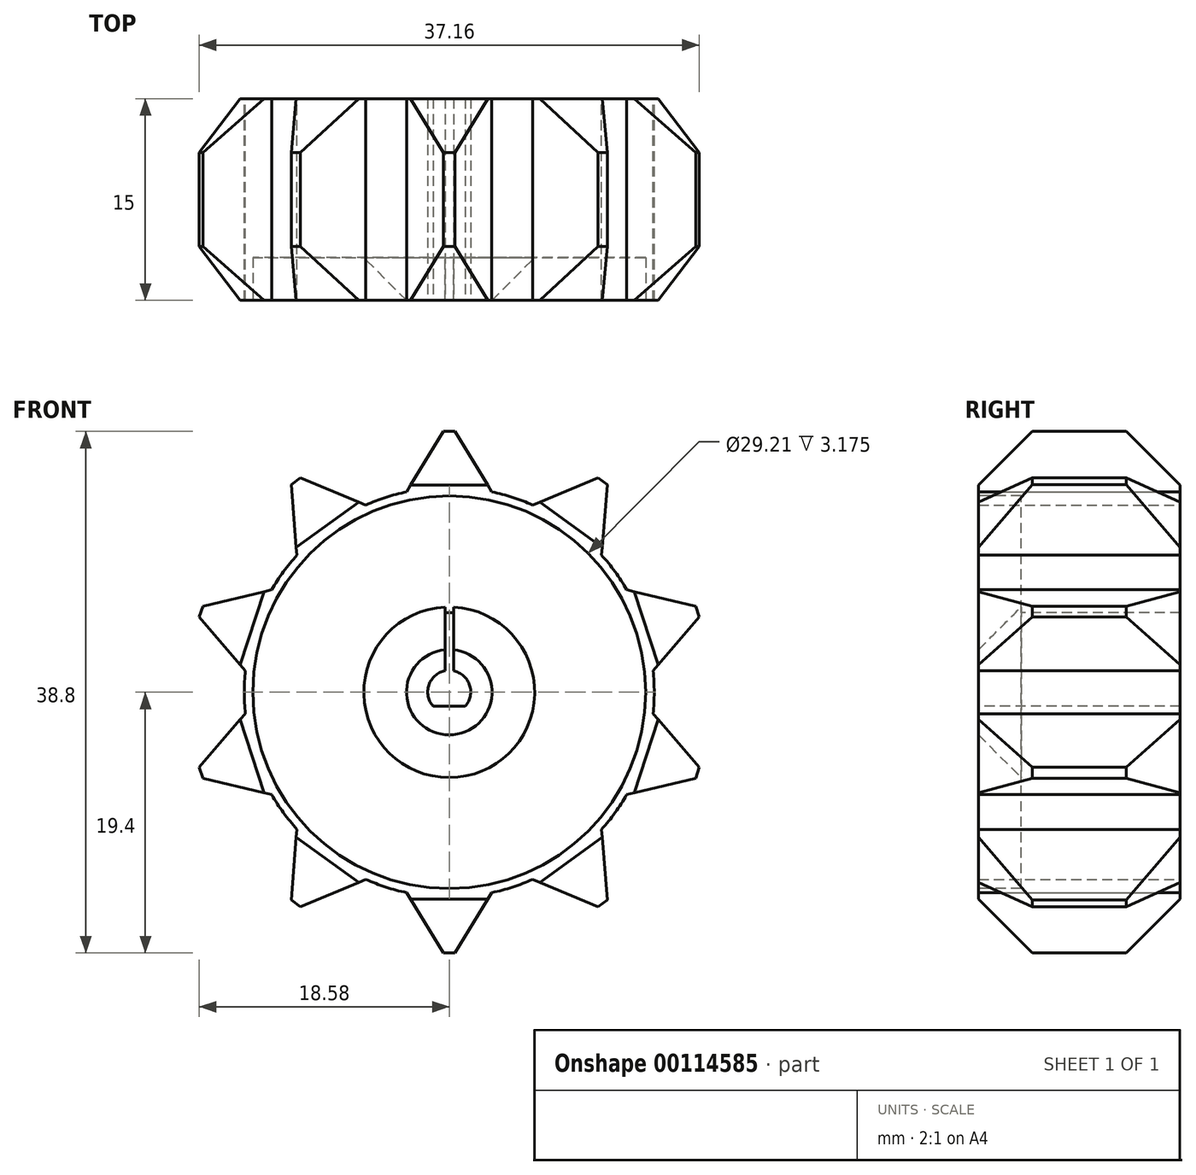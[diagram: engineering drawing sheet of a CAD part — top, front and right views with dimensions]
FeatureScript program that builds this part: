
annotation { "Feature Type Name" : "Feature", "Feature Type Description" : "" }
export const myFeature = defineFeature(function(context is Context, id is Id, definition is map)
    precondition{}
    {
        {
            var Q0;
            Q0=qCreatedBy(makeId("Front.planeOp"),FACE);
            var sketch = newSketch(context, id + "F0", { "sketchPlane" : qUnion([Q0])});
            skCircle(sketch, "E0", {"center": v(0, 0) * mm, "radius": 15.24 * mm});
            skLineSegment(sketch, "E1", {"start": v(0, 20.1) * mm, "end": v(3.17, 14.9) * mm});
            skLineSegment(sketch, "E2.MirrorCS", {"start": v(0, 20.1) * mm, "end": v(-3.17, 14.9) * mm});
            skLineSegment(sketch, "E3.1.0", {"start": v(-11.81, 16.26) * mm, "end": v(-11.32, 10.2) * mm});
            skLineSegment(sketch, "E3.1.1", {"start": v(-11.81, 16.26) * mm, "end": v(-6.2, 13.92) * mm});
            skLineSegment(sketch, "E3.2.0", {"start": v(-19.12, 6.21) * mm, "end": v(-15.16, 1.6) * mm});
            skLineSegment(sketch, "E3.2.1", {"start": v(-19.12, 6.21) * mm, "end": v(-13.2, 7.62) * mm});
            skLineSegment(sketch, "E4.2.3.0", {"start": v(-19.12, -6.21) * mm, "end": v(-13.2, -7.62) * mm});
            skLineSegment(sketch, "E4.3.3.0", {"start": v(-19.12, -6.21) * mm, "end": v(-15.16, -1.6) * mm});
            skLineSegment(sketch, "E4.2.4.0", {"start": v(-11.81, -16.26) * mm, "end": v(-6.2, -13.92) * mm});
            skLineSegment(sketch, "E4.3.4.0", {"start": v(-11.81, -16.26) * mm, "end": v(-11.32, -10.2) * mm});
            skLineSegment(sketch, "E4.2.5.0", {"start": v(0, -20.1) * mm, "end": v(3.17, -14.9) * mm});
            skLineSegment(sketch, "E4.3.5.0", {"start": v(0, -20.1) * mm, "end": v(-3.17, -14.9) * mm});
            skLineSegment(sketch, "E5.2.6.0", {"start": v(11.81, -16.26) * mm, "end": v(11.32, -10.2) * mm});
            skLineSegment(sketch, "E5.3.6.0", {"start": v(11.81, -16.26) * mm, "end": v(6.2, -13.92) * mm});
            skLineSegment(sketch, "E5.2.7.0", {"start": v(19.12, -6.21) * mm, "end": v(15.16, -1.6) * mm});
            skLineSegment(sketch, "E5.3.7.0", {"start": v(19.12, -6.21) * mm, "end": v(13.2, -7.62) * mm});
            skLineSegment(sketch, "E6.2.8.0", {"start": v(19.12, 6.21) * mm, "end": v(13.2, 7.62) * mm});
            skLineSegment(sketch, "E6.3.8.0", {"start": v(19.12, 6.21) * mm, "end": v(15.16, 1.6) * mm});
            skLineSegment(sketch, "E6.2.9.0", {"start": v(11.81, 16.26) * mm, "end": v(6.2, 13.92) * mm});
            skLineSegment(sketch, "E6.3.9.0", {"start": v(11.81, 16.26) * mm, "end": v(11.32, 10.2) * mm});
            skSolve(sketch);
        }
        {
            var Q0;
            {var subQ0=sQuery(id+"F0.wireOp",EDGE,"E4.2.5.0");Q0=makeQuery(id+"F0.imprint","IMPRINT",FACE,{"disambiguationData":[TD([[makeQuery(id+"F0.imprint","IMPRINT",EDGE,{"derivedFrom":subQ0}),1.0]])]});}
            var Q1;
            {var subQ0=sQuery(id+"F0.wireOp",EDGE,"E1");Q1=makeQuery(id+"F0.imprint","IMPRINT",FACE,{"disambiguationData":[TD([[makeQuery(id+"F0.imprint","IMPRINT",EDGE,{"derivedFrom":subQ0}),-1.0]])]});}
            var Q2;
            {var subQ0=sQuery(id+"F0.wireOp",EDGE,"E3.1.0");Q2=makeQuery(id+"F0.imprint","IMPRINT",FACE,{"disambiguationData":[TD([[makeQuery(id+"F0.imprint","IMPRINT",EDGE,{"derivedFrom":subQ0}),1.0]])]});}
            var Q3;
            {var subQ0=sQuery(id+"F0.wireOp",EDGE,"E3.2.0");Q3=makeQuery(id+"F0.imprint","IMPRINT",FACE,{"disambiguationData":[TD([[makeQuery(id+"F0.imprint","IMPRINT",EDGE,{"derivedFrom":subQ0}),1.0]])]});}
            var Q4;
            {var subQ0=sQuery(id+"F0.wireOp",EDGE,"E4.2.3.0");Q4=makeQuery(id+"F0.imprint","IMPRINT",FACE,{"disambiguationData":[TD([[makeQuery(id+"F0.imprint","IMPRINT",EDGE,{"derivedFrom":subQ0}),1.0]])]});}
            var Q5;
            {var subQ0=sQuery(id+"F0.wireOp",EDGE,"E4.2.4.0");Q5=makeQuery(id+"F0.imprint","IMPRINT",FACE,{"disambiguationData":[TD([[makeQuery(id+"F0.imprint","IMPRINT",EDGE,{"derivedFrom":subQ0}),1.0]])]});}
            var Q6;
            {var subQ0=sQuery(id+"F0.wireOp",EDGE,"E0");var subQ3=makeQuery(id+"F0.imprint","INTERSECT",VERTEX,{"derivedFrom":[subQ0,sQuery(id+"F0.wireOp",EDGE,"E4.2.5.0")]});Q6=makeQuery(id+"F0.imprint","IMPRINT",FACE,{"disambiguationData":[TD([[makeQuery(id+"F0.imprint","IMPRINT",EDGE,{"disambiguationData":[TD([[subQ3,1.0]])],"derivedFrom":subQ0}),1.0]])]});}
            var Q7;
            {var subQ0=sQuery(id+"F0.wireOp",EDGE,"E6.2.9.0");Q7=makeQuery(id+"F0.imprint","IMPRINT",FACE,{"disambiguationData":[TD([[makeQuery(id+"F0.imprint","IMPRINT",EDGE,{"derivedFrom":subQ0}),1.0]])]});}
            var Q8;
            {var subQ0=sQuery(id+"F0.wireOp",EDGE,"E6.2.8.0");Q8=makeQuery(id+"F0.imprint","IMPRINT",FACE,{"disambiguationData":[TD([[makeQuery(id+"F0.imprint","IMPRINT",EDGE,{"derivedFrom":subQ0}),1.0]])]});}
            var Q9;
            {var subQ0=sQuery(id+"F0.wireOp",EDGE,"E5.2.7.0");Q9=makeQuery(id+"F0.imprint","IMPRINT",FACE,{"disambiguationData":[TD([[makeQuery(id+"F0.imprint","IMPRINT",EDGE,{"derivedFrom":subQ0}),1.0]])]});}
            var Q10;
            {var subQ0=sQuery(id+"F0.wireOp",EDGE,"E5.2.6.0");Q10=makeQuery(id+"F0.imprint","IMPRINT",FACE,{"disambiguationData":[TD([[makeQuery(id+"F0.imprint","IMPRINT",EDGE,{"derivedFrom":subQ0}),1.0]])]});}
            extrude(context, id + "F1", {"entities" : qUnion([Q0, Q1, Q2, Q3, Q4, Q5, Q6, Q7, Q8, Q9, Q10]), "depth" : 15 * mm});
        }
        {
            var Q0;
            Q0=makeQuery(id+"F1.opExtrude","SWEPT_EDGE",EDGE,{"disambiguationData":[OSD([sQuery(id+"F0.wireOp",EDGE,"E4.2.5.0"),sQuery(id+"F0.wireOp",EDGE,"E4.3.5.0")])]});
            var Q1;
            Q1=makeQuery(id+"F1.opExtrude","SWEPT_EDGE",EDGE,{"disambiguationData":[OSD([sQuery(id+"F0.wireOp",EDGE,"E1"),sQuery(id+"F0.wireOp",EDGE,"E2.MirrorCS")])]});
            var Q2;
            Q2=makeQuery(id+"F1.opExtrude","SWEPT_EDGE",EDGE,{"disambiguationData":[OSD([sQuery(id+"F0.wireOp",EDGE,"E4.2.4.0"),sQuery(id+"F0.wireOp",EDGE,"E4.3.4.0")])]});
            var Q3;
            Q3=makeQuery(id+"F1.opExtrude","SWEPT_EDGE",EDGE,{"disambiguationData":[OSD([sQuery(id+"F0.wireOp",EDGE,"E4.2.3.0"),sQuery(id+"F0.wireOp",EDGE,"E4.3.3.0")])]});
            var Q4;
            Q4=makeQuery(id+"F1.opExtrude","SWEPT_EDGE",EDGE,{"disambiguationData":[OSD([sQuery(id+"F0.wireOp",EDGE,"E3.2.0"),sQuery(id+"F0.wireOp",EDGE,"E3.2.1")])]});
            var Q5;
            Q5=makeQuery(id+"F1.opExtrude","SWEPT_EDGE",EDGE,{"disambiguationData":[OSD([sQuery(id+"F0.wireOp",EDGE,"E3.1.0"),sQuery(id+"F0.wireOp",EDGE,"E3.1.1")])]});
            var Q6;
            Q6=makeQuery(id+"F1.opExtrude","SWEPT_EDGE",EDGE,{"disambiguationData":[OSD([sQuery(id+"F0.wireOp",EDGE,"E6.2.9.0"),sQuery(id+"F0.wireOp",EDGE,"E6.3.9.0")])]});
            var Q7;
            Q7=makeQuery(id+"F1.opExtrude","SWEPT_EDGE",EDGE,{"disambiguationData":[OSD([sQuery(id+"F0.wireOp",EDGE,"E6.2.8.0"),sQuery(id+"F0.wireOp",EDGE,"E6.3.8.0")])]});
            var Q8;
            Q8=makeQuery(id+"F1.opExtrude","SWEPT_EDGE",EDGE,{"disambiguationData":[OSD([sQuery(id+"F0.wireOp",EDGE,"E5.2.7.0"),sQuery(id+"F0.wireOp",EDGE,"E5.3.7.0")])]});
            var Q9;
            Q9=makeQuery(id+"F1.opExtrude","SWEPT_EDGE",EDGE,{"disambiguationData":[OSD([sQuery(id+"F0.wireOp",EDGE,"E5.2.6.0"),sQuery(id+"F0.wireOp",EDGE,"E5.3.6.0")])]});
            chamfer(context, id + "F2", {"entities" : qUnion([Q0, Q1, Q2, Q3, Q4, Q5, Q6, Q7, Q8, Q9]), "width" : .5 * mm, "tangentPropagation" : true});
        }
        {
            var Q0;
            {var subQ0=sQuery(id+"F0.wireOp",EDGE,"E3.1.1");var subQ1=sQuery(id+"F0.wireOp",EDGE,"E3.1.0");Q0=makeQuery(id+"F2.opChamfer","BLEND_EDGE",EDGE,{"blendedFrom":[makeQuery(id+"F1.opExtrude","SWEPT_EDGE",EDGE,{"disambiguationData":[OSD([subQ1,subQ0])]}),makeQuery(id+"F1.opExtrude","CAP_FACE",FACE,{"disambiguationData":[OSD([sQuery(id+"F0.wireOp",EDGE,"E0"),sQuery(id+"F0.wireOp",EDGE,"E1"),sQuery(id+"F0.wireOp",EDGE,"E2.MirrorCS"),subQ1,subQ0,sQuery(id+"F0.wireOp",EDGE,"E3.2.0"),sQuery(id+"F0.wireOp",EDGE,"E3.2.1"),sQuery(id+"F0.wireOp",EDGE,"E4.2.3.0"),sQuery(id+"F0.wireOp",EDGE,"E4.3.3.0"),sQuery(id+"F0.wireOp",EDGE,"E4.2.4.0"),sQuery(id+"F0.wireOp",EDGE,"E4.3.4.0"),sQuery(id+"F0.wireOp",EDGE,"E4.2.5.0"),sQuery(id+"F0.wireOp",EDGE,"E4.3.5.0")])],"isStart":false})],"blendedInto":[makeQuery(id+"F1.opExtrude","CAP_FACE",FACE,{"disambiguationData":[OSD([sQuery(id+"F0.wireOp",EDGE,"E0"),sQuery(id+"F0.wireOp",EDGE,"E1"),sQuery(id+"F0.wireOp",EDGE,"E2.MirrorCS"),subQ1,subQ0,sQuery(id+"F0.wireOp",EDGE,"E3.2.0"),sQuery(id+"F0.wireOp",EDGE,"E3.2.1"),sQuery(id+"F0.wireOp",EDGE,"E4.2.3.0"),sQuery(id+"F0.wireOp",EDGE,"E4.3.3.0"),sQuery(id+"F0.wireOp",EDGE,"E4.2.4.0"),sQuery(id+"F0.wireOp",EDGE,"E4.3.4.0"),sQuery(id+"F0.wireOp",EDGE,"E4.2.5.0"),sQuery(id+"F0.wireOp",EDGE,"E4.3.5.0")])],"isStart":false})]});}
            var Q1;
            {var subQ0=sQuery(id+"F0.wireOp",EDGE,"E3.1.1");var subQ1=sQuery(id+"F0.wireOp",EDGE,"E3.1.0");Q1=makeQuery(id+"F2.opChamfer","BLEND_EDGE",EDGE,{"blendedFrom":[makeQuery(id+"F1.opExtrude","SWEPT_EDGE",EDGE,{"disambiguationData":[OSD([subQ1,subQ0])]}),makeQuery(id+"F1.opExtrude","CAP_FACE",FACE,{"disambiguationData":[OSD([sQuery(id+"F0.wireOp",EDGE,"E0"),sQuery(id+"F0.wireOp",EDGE,"E1"),sQuery(id+"F0.wireOp",EDGE,"E2.MirrorCS"),subQ1,subQ0,sQuery(id+"F0.wireOp",EDGE,"E3.2.0"),sQuery(id+"F0.wireOp",EDGE,"E3.2.1"),sQuery(id+"F0.wireOp",EDGE,"E4.2.3.0"),sQuery(id+"F0.wireOp",EDGE,"E4.3.3.0"),sQuery(id+"F0.wireOp",EDGE,"E4.2.4.0"),sQuery(id+"F0.wireOp",EDGE,"E4.3.4.0"),sQuery(id+"F0.wireOp",EDGE,"E4.2.5.0"),sQuery(id+"F0.wireOp",EDGE,"E4.3.5.0")])],"isStart":true})],"blendedInto":[makeQuery(id+"F1.opExtrude","CAP_FACE",FACE,{"disambiguationData":[OSD([sQuery(id+"F0.wireOp",EDGE,"E0"),sQuery(id+"F0.wireOp",EDGE,"E1"),sQuery(id+"F0.wireOp",EDGE,"E2.MirrorCS"),subQ1,subQ0,sQuery(id+"F0.wireOp",EDGE,"E3.2.0"),sQuery(id+"F0.wireOp",EDGE,"E3.2.1"),sQuery(id+"F0.wireOp",EDGE,"E4.2.3.0"),sQuery(id+"F0.wireOp",EDGE,"E4.3.3.0"),sQuery(id+"F0.wireOp",EDGE,"E4.2.4.0"),sQuery(id+"F0.wireOp",EDGE,"E4.3.4.0"),sQuery(id+"F0.wireOp",EDGE,"E4.2.5.0"),sQuery(id+"F0.wireOp",EDGE,"E4.3.5.0")])],"isStart":true})]});}
            var Q2;
            {var subQ0=sQuery(id+"F0.wireOp",EDGE,"E2.MirrorCS");var subQ1=sQuery(id+"F0.wireOp",EDGE,"E1");Q2=makeQuery(id+"F2.opChamfer","BLEND_EDGE",EDGE,{"blendedFrom":[makeQuery(id+"F1.opExtrude","SWEPT_EDGE",EDGE,{"disambiguationData":[OSD([subQ1,subQ0])]}),makeQuery(id+"F1.opExtrude","CAP_FACE",FACE,{"disambiguationData":[OSD([sQuery(id+"F0.wireOp",EDGE,"E0"),subQ1,subQ0,sQuery(id+"F0.wireOp",EDGE,"E3.1.0"),sQuery(id+"F0.wireOp",EDGE,"E3.1.1"),sQuery(id+"F0.wireOp",EDGE,"E3.2.0"),sQuery(id+"F0.wireOp",EDGE,"E3.2.1"),sQuery(id+"F0.wireOp",EDGE,"E4.2.3.0"),sQuery(id+"F0.wireOp",EDGE,"E4.3.3.0"),sQuery(id+"F0.wireOp",EDGE,"E4.2.4.0"),sQuery(id+"F0.wireOp",EDGE,"E4.3.4.0"),sQuery(id+"F0.wireOp",EDGE,"E4.2.5.0"),sQuery(id+"F0.wireOp",EDGE,"E4.3.5.0")])],"isStart":true})],"blendedInto":[makeQuery(id+"F1.opExtrude","CAP_FACE",FACE,{"disambiguationData":[OSD([sQuery(id+"F0.wireOp",EDGE,"E0"),subQ1,subQ0,sQuery(id+"F0.wireOp",EDGE,"E3.1.0"),sQuery(id+"F0.wireOp",EDGE,"E3.1.1"),sQuery(id+"F0.wireOp",EDGE,"E3.2.0"),sQuery(id+"F0.wireOp",EDGE,"E3.2.1"),sQuery(id+"F0.wireOp",EDGE,"E4.2.3.0"),sQuery(id+"F0.wireOp",EDGE,"E4.3.3.0"),sQuery(id+"F0.wireOp",EDGE,"E4.2.4.0"),sQuery(id+"F0.wireOp",EDGE,"E4.3.4.0"),sQuery(id+"F0.wireOp",EDGE,"E4.2.5.0"),sQuery(id+"F0.wireOp",EDGE,"E4.3.5.0")])],"isStart":true})]});}
            var Q3;
            {var subQ0=sQuery(id+"F0.wireOp",EDGE,"E2.MirrorCS");var subQ1=sQuery(id+"F0.wireOp",EDGE,"E1");Q3=makeQuery(id+"F2.opChamfer","BLEND_EDGE",EDGE,{"blendedFrom":[makeQuery(id+"F1.opExtrude","SWEPT_EDGE",EDGE,{"disambiguationData":[OSD([subQ1,subQ0])]}),makeQuery(id+"F1.opExtrude","CAP_FACE",FACE,{"disambiguationData":[OSD([sQuery(id+"F0.wireOp",EDGE,"E0"),subQ1,subQ0,sQuery(id+"F0.wireOp",EDGE,"E3.1.0"),sQuery(id+"F0.wireOp",EDGE,"E3.1.1"),sQuery(id+"F0.wireOp",EDGE,"E3.2.0"),sQuery(id+"F0.wireOp",EDGE,"E3.2.1"),sQuery(id+"F0.wireOp",EDGE,"E4.2.3.0"),sQuery(id+"F0.wireOp",EDGE,"E4.3.3.0"),sQuery(id+"F0.wireOp",EDGE,"E4.2.4.0"),sQuery(id+"F0.wireOp",EDGE,"E4.3.4.0"),sQuery(id+"F0.wireOp",EDGE,"E4.2.5.0"),sQuery(id+"F0.wireOp",EDGE,"E4.3.5.0")])],"isStart":false})],"blendedInto":[makeQuery(id+"F1.opExtrude","CAP_FACE",FACE,{"disambiguationData":[OSD([sQuery(id+"F0.wireOp",EDGE,"E0"),subQ1,subQ0,sQuery(id+"F0.wireOp",EDGE,"E3.1.0"),sQuery(id+"F0.wireOp",EDGE,"E3.1.1"),sQuery(id+"F0.wireOp",EDGE,"E3.2.0"),sQuery(id+"F0.wireOp",EDGE,"E3.2.1"),sQuery(id+"F0.wireOp",EDGE,"E4.2.3.0"),sQuery(id+"F0.wireOp",EDGE,"E4.3.3.0"),sQuery(id+"F0.wireOp",EDGE,"E4.2.4.0"),sQuery(id+"F0.wireOp",EDGE,"E4.3.4.0"),sQuery(id+"F0.wireOp",EDGE,"E4.2.5.0"),sQuery(id+"F0.wireOp",EDGE,"E4.3.5.0")])],"isStart":false})]});}
            var Q4;
            {var subQ0=sQuery(id+"F0.wireOp",EDGE,"E4.3.5.0");var subQ1=sQuery(id+"F0.wireOp",EDGE,"E4.2.5.0");Q4=makeQuery(id+"F2.opChamfer","BLEND_EDGE",EDGE,{"blendedFrom":[makeQuery(id+"F1.opExtrude","SWEPT_EDGE",EDGE,{"disambiguationData":[OSD([subQ1,subQ0])]}),makeQuery(id+"F1.opExtrude","CAP_FACE",FACE,{"disambiguationData":[OSD([sQuery(id+"F0.wireOp",EDGE,"E0"),sQuery(id+"F0.wireOp",EDGE,"E1"),sQuery(id+"F0.wireOp",EDGE,"E2.MirrorCS"),sQuery(id+"F0.wireOp",EDGE,"E3.1.0"),sQuery(id+"F0.wireOp",EDGE,"E3.1.1"),sQuery(id+"F0.wireOp",EDGE,"E3.2.0"),sQuery(id+"F0.wireOp",EDGE,"E3.2.1"),sQuery(id+"F0.wireOp",EDGE,"E4.2.3.0"),sQuery(id+"F0.wireOp",EDGE,"E4.3.3.0"),sQuery(id+"F0.wireOp",EDGE,"E4.2.4.0"),sQuery(id+"F0.wireOp",EDGE,"E4.3.4.0"),subQ1,subQ0])],"isStart":false})],"blendedInto":[makeQuery(id+"F1.opExtrude","CAP_FACE",FACE,{"disambiguationData":[OSD([sQuery(id+"F0.wireOp",EDGE,"E0"),sQuery(id+"F0.wireOp",EDGE,"E1"),sQuery(id+"F0.wireOp",EDGE,"E2.MirrorCS"),sQuery(id+"F0.wireOp",EDGE,"E3.1.0"),sQuery(id+"F0.wireOp",EDGE,"E3.1.1"),sQuery(id+"F0.wireOp",EDGE,"E3.2.0"),sQuery(id+"F0.wireOp",EDGE,"E3.2.1"),sQuery(id+"F0.wireOp",EDGE,"E4.2.3.0"),sQuery(id+"F0.wireOp",EDGE,"E4.3.3.0"),sQuery(id+"F0.wireOp",EDGE,"E4.2.4.0"),sQuery(id+"F0.wireOp",EDGE,"E4.3.4.0"),subQ1,subQ0])],"isStart":false})]});}
            var Q5;
            {var subQ0=sQuery(id+"F0.wireOp",EDGE,"E4.3.4.0");var subQ1=sQuery(id+"F0.wireOp",EDGE,"E4.2.4.0");Q5=makeQuery(id+"F2.opChamfer","BLEND_EDGE",EDGE,{"blendedFrom":[makeQuery(id+"F1.opExtrude","SWEPT_EDGE",EDGE,{"disambiguationData":[OSD([subQ1,subQ0])]}),makeQuery(id+"F1.opExtrude","CAP_FACE",FACE,{"disambiguationData":[OSD([sQuery(id+"F0.wireOp",EDGE,"E0"),sQuery(id+"F0.wireOp",EDGE,"E1"),sQuery(id+"F0.wireOp",EDGE,"E2.MirrorCS"),sQuery(id+"F0.wireOp",EDGE,"E3.1.0"),sQuery(id+"F0.wireOp",EDGE,"E3.1.1"),sQuery(id+"F0.wireOp",EDGE,"E3.2.0"),sQuery(id+"F0.wireOp",EDGE,"E3.2.1"),sQuery(id+"F0.wireOp",EDGE,"E4.2.3.0"),sQuery(id+"F0.wireOp",EDGE,"E4.3.3.0"),subQ1,subQ0,sQuery(id+"F0.wireOp",EDGE,"E4.2.5.0"),sQuery(id+"F0.wireOp",EDGE,"E4.3.5.0")])],"isStart":false})],"blendedInto":[makeQuery(id+"F1.opExtrude","CAP_FACE",FACE,{"disambiguationData":[OSD([sQuery(id+"F0.wireOp",EDGE,"E0"),sQuery(id+"F0.wireOp",EDGE,"E1"),sQuery(id+"F0.wireOp",EDGE,"E2.MirrorCS"),sQuery(id+"F0.wireOp",EDGE,"E3.1.0"),sQuery(id+"F0.wireOp",EDGE,"E3.1.1"),sQuery(id+"F0.wireOp",EDGE,"E3.2.0"),sQuery(id+"F0.wireOp",EDGE,"E3.2.1"),sQuery(id+"F0.wireOp",EDGE,"E4.2.3.0"),sQuery(id+"F0.wireOp",EDGE,"E4.3.3.0"),subQ1,subQ0,sQuery(id+"F0.wireOp",EDGE,"E4.2.5.0"),sQuery(id+"F0.wireOp",EDGE,"E4.3.5.0")])],"isStart":false})]});}
            var Q6;
            {var subQ0=sQuery(id+"F0.wireOp",EDGE,"E4.3.3.0");var subQ1=sQuery(id+"F0.wireOp",EDGE,"E4.2.3.0");Q6=makeQuery(id+"F2.opChamfer","BLEND_EDGE",EDGE,{"blendedFrom":[makeQuery(id+"F1.opExtrude","SWEPT_EDGE",EDGE,{"disambiguationData":[OSD([subQ1,subQ0])]}),makeQuery(id+"F1.opExtrude","CAP_FACE",FACE,{"disambiguationData":[OSD([sQuery(id+"F0.wireOp",EDGE,"E0"),sQuery(id+"F0.wireOp",EDGE,"E1"),sQuery(id+"F0.wireOp",EDGE,"E2.MirrorCS"),sQuery(id+"F0.wireOp",EDGE,"E3.1.0"),sQuery(id+"F0.wireOp",EDGE,"E3.1.1"),sQuery(id+"F0.wireOp",EDGE,"E3.2.0"),sQuery(id+"F0.wireOp",EDGE,"E3.2.1"),subQ1,subQ0,sQuery(id+"F0.wireOp",EDGE,"E4.2.4.0"),sQuery(id+"F0.wireOp",EDGE,"E4.3.4.0"),sQuery(id+"F0.wireOp",EDGE,"E4.2.5.0"),sQuery(id+"F0.wireOp",EDGE,"E4.3.5.0")])],"isStart":false})],"blendedInto":[makeQuery(id+"F1.opExtrude","CAP_FACE",FACE,{"disambiguationData":[OSD([sQuery(id+"F0.wireOp",EDGE,"E0"),sQuery(id+"F0.wireOp",EDGE,"E1"),sQuery(id+"F0.wireOp",EDGE,"E2.MirrorCS"),sQuery(id+"F0.wireOp",EDGE,"E3.1.0"),sQuery(id+"F0.wireOp",EDGE,"E3.1.1"),sQuery(id+"F0.wireOp",EDGE,"E3.2.0"),sQuery(id+"F0.wireOp",EDGE,"E3.2.1"),subQ1,subQ0,sQuery(id+"F0.wireOp",EDGE,"E4.2.4.0"),sQuery(id+"F0.wireOp",EDGE,"E4.3.4.0"),sQuery(id+"F0.wireOp",EDGE,"E4.2.5.0"),sQuery(id+"F0.wireOp",EDGE,"E4.3.5.0")])],"isStart":false})]});}
            var Q7;
            {var subQ0=sQuery(id+"F0.wireOp",EDGE,"E3.2.1");var subQ1=sQuery(id+"F0.wireOp",EDGE,"E3.2.0");Q7=makeQuery(id+"F2.opChamfer","BLEND_EDGE",EDGE,{"blendedFrom":[makeQuery(id+"F1.opExtrude","SWEPT_EDGE",EDGE,{"disambiguationData":[OSD([subQ1,subQ0])]}),makeQuery(id+"F1.opExtrude","CAP_FACE",FACE,{"disambiguationData":[OSD([sQuery(id+"F0.wireOp",EDGE,"E0"),sQuery(id+"F0.wireOp",EDGE,"E1"),sQuery(id+"F0.wireOp",EDGE,"E2.MirrorCS"),sQuery(id+"F0.wireOp",EDGE,"E3.1.0"),sQuery(id+"F0.wireOp",EDGE,"E3.1.1"),subQ1,subQ0,sQuery(id+"F0.wireOp",EDGE,"E4.2.3.0"),sQuery(id+"F0.wireOp",EDGE,"E4.3.3.0"),sQuery(id+"F0.wireOp",EDGE,"E4.2.4.0"),sQuery(id+"F0.wireOp",EDGE,"E4.3.4.0"),sQuery(id+"F0.wireOp",EDGE,"E4.2.5.0"),sQuery(id+"F0.wireOp",EDGE,"E4.3.5.0")])],"isStart":false})],"blendedInto":[makeQuery(id+"F1.opExtrude","CAP_FACE",FACE,{"disambiguationData":[OSD([sQuery(id+"F0.wireOp",EDGE,"E0"),sQuery(id+"F0.wireOp",EDGE,"E1"),sQuery(id+"F0.wireOp",EDGE,"E2.MirrorCS"),sQuery(id+"F0.wireOp",EDGE,"E3.1.0"),sQuery(id+"F0.wireOp",EDGE,"E3.1.1"),subQ1,subQ0,sQuery(id+"F0.wireOp",EDGE,"E4.2.3.0"),sQuery(id+"F0.wireOp",EDGE,"E4.3.3.0"),sQuery(id+"F0.wireOp",EDGE,"E4.2.4.0"),sQuery(id+"F0.wireOp",EDGE,"E4.3.4.0"),sQuery(id+"F0.wireOp",EDGE,"E4.2.5.0"),sQuery(id+"F0.wireOp",EDGE,"E4.3.5.0")])],"isStart":false})]});}
            var Q8;
            {var subQ0=sQuery(id+"F0.wireOp",EDGE,"E3.2.1");var subQ1=sQuery(id+"F0.wireOp",EDGE,"E3.2.0");Q8=makeQuery(id+"F2.opChamfer","BLEND_EDGE",EDGE,{"blendedFrom":[makeQuery(id+"F1.opExtrude","SWEPT_EDGE",EDGE,{"disambiguationData":[OSD([subQ1,subQ0])]}),makeQuery(id+"F1.opExtrude","CAP_FACE",FACE,{"disambiguationData":[OSD([sQuery(id+"F0.wireOp",EDGE,"E0"),sQuery(id+"F0.wireOp",EDGE,"E1"),sQuery(id+"F0.wireOp",EDGE,"E2.MirrorCS"),sQuery(id+"F0.wireOp",EDGE,"E3.1.0"),sQuery(id+"F0.wireOp",EDGE,"E3.1.1"),subQ1,subQ0,sQuery(id+"F0.wireOp",EDGE,"E4.2.3.0"),sQuery(id+"F0.wireOp",EDGE,"E4.3.3.0"),sQuery(id+"F0.wireOp",EDGE,"E4.2.4.0"),sQuery(id+"F0.wireOp",EDGE,"E4.3.4.0"),sQuery(id+"F0.wireOp",EDGE,"E4.2.5.0"),sQuery(id+"F0.wireOp",EDGE,"E4.3.5.0")])],"isStart":true})],"blendedInto":[makeQuery(id+"F1.opExtrude","CAP_FACE",FACE,{"disambiguationData":[OSD([sQuery(id+"F0.wireOp",EDGE,"E0"),sQuery(id+"F0.wireOp",EDGE,"E1"),sQuery(id+"F0.wireOp",EDGE,"E2.MirrorCS"),sQuery(id+"F0.wireOp",EDGE,"E3.1.0"),sQuery(id+"F0.wireOp",EDGE,"E3.1.1"),subQ1,subQ0,sQuery(id+"F0.wireOp",EDGE,"E4.2.3.0"),sQuery(id+"F0.wireOp",EDGE,"E4.3.3.0"),sQuery(id+"F0.wireOp",EDGE,"E4.2.4.0"),sQuery(id+"F0.wireOp",EDGE,"E4.3.4.0"),sQuery(id+"F0.wireOp",EDGE,"E4.2.5.0"),sQuery(id+"F0.wireOp",EDGE,"E4.3.5.0")])],"isStart":true})]});}
            var Q9;
            {var subQ0=sQuery(id+"F0.wireOp",EDGE,"E4.3.3.0");var subQ1=sQuery(id+"F0.wireOp",EDGE,"E4.2.3.0");Q9=makeQuery(id+"F2.opChamfer","BLEND_EDGE",EDGE,{"blendedFrom":[makeQuery(id+"F1.opExtrude","SWEPT_EDGE",EDGE,{"disambiguationData":[OSD([subQ1,subQ0])]}),makeQuery(id+"F1.opExtrude","CAP_FACE",FACE,{"disambiguationData":[OSD([sQuery(id+"F0.wireOp",EDGE,"E0"),sQuery(id+"F0.wireOp",EDGE,"E1"),sQuery(id+"F0.wireOp",EDGE,"E2.MirrorCS"),sQuery(id+"F0.wireOp",EDGE,"E3.1.0"),sQuery(id+"F0.wireOp",EDGE,"E3.1.1"),sQuery(id+"F0.wireOp",EDGE,"E3.2.0"),sQuery(id+"F0.wireOp",EDGE,"E3.2.1"),subQ1,subQ0,sQuery(id+"F0.wireOp",EDGE,"E4.2.4.0"),sQuery(id+"F0.wireOp",EDGE,"E4.3.4.0"),sQuery(id+"F0.wireOp",EDGE,"E4.2.5.0"),sQuery(id+"F0.wireOp",EDGE,"E4.3.5.0")])],"isStart":true})],"blendedInto":[makeQuery(id+"F1.opExtrude","CAP_FACE",FACE,{"disambiguationData":[OSD([sQuery(id+"F0.wireOp",EDGE,"E0"),sQuery(id+"F0.wireOp",EDGE,"E1"),sQuery(id+"F0.wireOp",EDGE,"E2.MirrorCS"),sQuery(id+"F0.wireOp",EDGE,"E3.1.0"),sQuery(id+"F0.wireOp",EDGE,"E3.1.1"),sQuery(id+"F0.wireOp",EDGE,"E3.2.0"),sQuery(id+"F0.wireOp",EDGE,"E3.2.1"),subQ1,subQ0,sQuery(id+"F0.wireOp",EDGE,"E4.2.4.0"),sQuery(id+"F0.wireOp",EDGE,"E4.3.4.0"),sQuery(id+"F0.wireOp",EDGE,"E4.2.5.0"),sQuery(id+"F0.wireOp",EDGE,"E4.3.5.0")])],"isStart":true})]});}
            var Q10;
            {var subQ0=sQuery(id+"F0.wireOp",EDGE,"E4.3.4.0");var subQ1=sQuery(id+"F0.wireOp",EDGE,"E4.2.4.0");Q10=makeQuery(id+"F2.opChamfer","BLEND_EDGE",EDGE,{"blendedFrom":[makeQuery(id+"F1.opExtrude","SWEPT_EDGE",EDGE,{"disambiguationData":[OSD([subQ1,subQ0])]}),makeQuery(id+"F1.opExtrude","CAP_FACE",FACE,{"disambiguationData":[OSD([sQuery(id+"F0.wireOp",EDGE,"E0"),sQuery(id+"F0.wireOp",EDGE,"E1"),sQuery(id+"F0.wireOp",EDGE,"E2.MirrorCS"),sQuery(id+"F0.wireOp",EDGE,"E3.1.0"),sQuery(id+"F0.wireOp",EDGE,"E3.1.1"),sQuery(id+"F0.wireOp",EDGE,"E3.2.0"),sQuery(id+"F0.wireOp",EDGE,"E3.2.1"),sQuery(id+"F0.wireOp",EDGE,"E4.2.3.0"),sQuery(id+"F0.wireOp",EDGE,"E4.3.3.0"),subQ1,subQ0,sQuery(id+"F0.wireOp",EDGE,"E4.2.5.0"),sQuery(id+"F0.wireOp",EDGE,"E4.3.5.0")])],"isStart":true})],"blendedInto":[makeQuery(id+"F1.opExtrude","CAP_FACE",FACE,{"disambiguationData":[OSD([sQuery(id+"F0.wireOp",EDGE,"E0"),sQuery(id+"F0.wireOp",EDGE,"E1"),sQuery(id+"F0.wireOp",EDGE,"E2.MirrorCS"),sQuery(id+"F0.wireOp",EDGE,"E3.1.0"),sQuery(id+"F0.wireOp",EDGE,"E3.1.1"),sQuery(id+"F0.wireOp",EDGE,"E3.2.0"),sQuery(id+"F0.wireOp",EDGE,"E3.2.1"),sQuery(id+"F0.wireOp",EDGE,"E4.2.3.0"),sQuery(id+"F0.wireOp",EDGE,"E4.3.3.0"),subQ1,subQ0,sQuery(id+"F0.wireOp",EDGE,"E4.2.5.0"),sQuery(id+"F0.wireOp",EDGE,"E4.3.5.0")])],"isStart":true})]});}
            var Q11;
            {var subQ0=sQuery(id+"F0.wireOp",EDGE,"E4.3.5.0");var subQ1=sQuery(id+"F0.wireOp",EDGE,"E4.2.5.0");Q11=makeQuery(id+"F2.opChamfer","BLEND_EDGE",EDGE,{"blendedFrom":[makeQuery(id+"F1.opExtrude","SWEPT_EDGE",EDGE,{"disambiguationData":[OSD([subQ1,subQ0])]}),makeQuery(id+"F1.opExtrude","CAP_FACE",FACE,{"disambiguationData":[OSD([sQuery(id+"F0.wireOp",EDGE,"E0"),sQuery(id+"F0.wireOp",EDGE,"E1"),sQuery(id+"F0.wireOp",EDGE,"E2.MirrorCS"),sQuery(id+"F0.wireOp",EDGE,"E3.1.0"),sQuery(id+"F0.wireOp",EDGE,"E3.1.1"),sQuery(id+"F0.wireOp",EDGE,"E3.2.0"),sQuery(id+"F0.wireOp",EDGE,"E3.2.1"),sQuery(id+"F0.wireOp",EDGE,"E4.2.3.0"),sQuery(id+"F0.wireOp",EDGE,"E4.3.3.0"),sQuery(id+"F0.wireOp",EDGE,"E4.2.4.0"),sQuery(id+"F0.wireOp",EDGE,"E4.3.4.0"),subQ1,subQ0])],"isStart":true})],"blendedInto":[makeQuery(id+"F1.opExtrude","CAP_FACE",FACE,{"disambiguationData":[OSD([sQuery(id+"F0.wireOp",EDGE,"E0"),sQuery(id+"F0.wireOp",EDGE,"E1"),sQuery(id+"F0.wireOp",EDGE,"E2.MirrorCS"),sQuery(id+"F0.wireOp",EDGE,"E3.1.0"),sQuery(id+"F0.wireOp",EDGE,"E3.1.1"),sQuery(id+"F0.wireOp",EDGE,"E3.2.0"),sQuery(id+"F0.wireOp",EDGE,"E3.2.1"),sQuery(id+"F0.wireOp",EDGE,"E4.2.3.0"),sQuery(id+"F0.wireOp",EDGE,"E4.3.3.0"),sQuery(id+"F0.wireOp",EDGE,"E4.2.4.0"),sQuery(id+"F0.wireOp",EDGE,"E4.3.4.0"),subQ1,subQ0])],"isStart":true})]});}
            var Q12;
            {var subQ0=sQuery(id+"F0.wireOp",EDGE,"E6.3.9.0");var subQ1=sQuery(id+"F0.wireOp",EDGE,"E6.2.9.0");Q12=makeQuery(id+"F2.opChamfer","BLEND_EDGE",EDGE,{"blendedFrom":[makeQuery(id+"F1.opExtrude","SWEPT_EDGE",EDGE,{"disambiguationData":[OSD([subQ1,subQ0])]}),makeQuery(id+"F1.opExtrude","CAP_FACE",FACE,{"disambiguationData":[OSD([sQuery(id+"F0.wireOp",EDGE,"E0"),sQuery(id+"F0.wireOp",EDGE,"E1"),sQuery(id+"F0.wireOp",EDGE,"E2.MirrorCS"),sQuery(id+"F0.wireOp",EDGE,"E3.1.0"),sQuery(id+"F0.wireOp",EDGE,"E3.1.1"),sQuery(id+"F0.wireOp",EDGE,"E3.2.0"),sQuery(id+"F0.wireOp",EDGE,"E3.2.1"),sQuery(id+"F0.wireOp",EDGE,"E4.2.3.0"),sQuery(id+"F0.wireOp",EDGE,"E4.3.3.0"),sQuery(id+"F0.wireOp",EDGE,"E4.2.4.0"),sQuery(id+"F0.wireOp",EDGE,"E4.3.4.0"),sQuery(id+"F0.wireOp",EDGE,"E4.2.5.0"),sQuery(id+"F0.wireOp",EDGE,"E4.3.5.0"),sQuery(id+"F0.wireOp",EDGE,"E5.2.6.0"),sQuery(id+"F0.wireOp",EDGE,"E5.3.6.0"),sQuery(id+"F0.wireOp",EDGE,"E5.2.7.0"),sQuery(id+"F0.wireOp",EDGE,"E5.3.7.0"),sQuery(id+"F0.wireOp",EDGE,"E6.2.8.0"),sQuery(id+"F0.wireOp",EDGE,"E6.3.8.0"),subQ1,subQ0])],"isStart":false})],"blendedInto":[makeQuery(id+"F1.opExtrude","CAP_FACE",FACE,{"disambiguationData":[OSD([sQuery(id+"F0.wireOp",EDGE,"E0"),sQuery(id+"F0.wireOp",EDGE,"E1"),sQuery(id+"F0.wireOp",EDGE,"E2.MirrorCS"),sQuery(id+"F0.wireOp",EDGE,"E3.1.0"),sQuery(id+"F0.wireOp",EDGE,"E3.1.1"),sQuery(id+"F0.wireOp",EDGE,"E3.2.0"),sQuery(id+"F0.wireOp",EDGE,"E3.2.1"),sQuery(id+"F0.wireOp",EDGE,"E4.2.3.0"),sQuery(id+"F0.wireOp",EDGE,"E4.3.3.0"),sQuery(id+"F0.wireOp",EDGE,"E4.2.4.0"),sQuery(id+"F0.wireOp",EDGE,"E4.3.4.0"),sQuery(id+"F0.wireOp",EDGE,"E4.2.5.0"),sQuery(id+"F0.wireOp",EDGE,"E4.3.5.0"),sQuery(id+"F0.wireOp",EDGE,"E5.2.6.0"),sQuery(id+"F0.wireOp",EDGE,"E5.3.6.0"),sQuery(id+"F0.wireOp",EDGE,"E5.2.7.0"),sQuery(id+"F0.wireOp",EDGE,"E5.3.7.0"),sQuery(id+"F0.wireOp",EDGE,"E6.2.8.0"),sQuery(id+"F0.wireOp",EDGE,"E6.3.8.0"),subQ1,subQ0])],"isStart":false})]});}
            var Q13;
            {var subQ0=sQuery(id+"F0.wireOp",EDGE,"E6.3.8.0");var subQ1=sQuery(id+"F0.wireOp",EDGE,"E6.2.8.0");Q13=makeQuery(id+"F2.opChamfer","BLEND_EDGE",EDGE,{"blendedFrom":[makeQuery(id+"F1.opExtrude","SWEPT_EDGE",EDGE,{"disambiguationData":[OSD([subQ1,subQ0])]}),makeQuery(id+"F1.opExtrude","CAP_FACE",FACE,{"disambiguationData":[OSD([sQuery(id+"F0.wireOp",EDGE,"E0"),sQuery(id+"F0.wireOp",EDGE,"E1"),sQuery(id+"F0.wireOp",EDGE,"E2.MirrorCS"),sQuery(id+"F0.wireOp",EDGE,"E3.1.0"),sQuery(id+"F0.wireOp",EDGE,"E3.1.1"),sQuery(id+"F0.wireOp",EDGE,"E3.2.0"),sQuery(id+"F0.wireOp",EDGE,"E3.2.1"),sQuery(id+"F0.wireOp",EDGE,"E4.2.3.0"),sQuery(id+"F0.wireOp",EDGE,"E4.3.3.0"),sQuery(id+"F0.wireOp",EDGE,"E4.2.4.0"),sQuery(id+"F0.wireOp",EDGE,"E4.3.4.0"),sQuery(id+"F0.wireOp",EDGE,"E4.2.5.0"),sQuery(id+"F0.wireOp",EDGE,"E4.3.5.0"),sQuery(id+"F0.wireOp",EDGE,"E5.2.6.0"),sQuery(id+"F0.wireOp",EDGE,"E5.3.6.0"),sQuery(id+"F0.wireOp",EDGE,"E5.2.7.0"),sQuery(id+"F0.wireOp",EDGE,"E5.3.7.0"),subQ1,subQ0,sQuery(id+"F0.wireOp",EDGE,"E6.2.9.0"),sQuery(id+"F0.wireOp",EDGE,"E6.3.9.0")])],"isStart":false})],"blendedInto":[makeQuery(id+"F1.opExtrude","CAP_FACE",FACE,{"disambiguationData":[OSD([sQuery(id+"F0.wireOp",EDGE,"E0"),sQuery(id+"F0.wireOp",EDGE,"E1"),sQuery(id+"F0.wireOp",EDGE,"E2.MirrorCS"),sQuery(id+"F0.wireOp",EDGE,"E3.1.0"),sQuery(id+"F0.wireOp",EDGE,"E3.1.1"),sQuery(id+"F0.wireOp",EDGE,"E3.2.0"),sQuery(id+"F0.wireOp",EDGE,"E3.2.1"),sQuery(id+"F0.wireOp",EDGE,"E4.2.3.0"),sQuery(id+"F0.wireOp",EDGE,"E4.3.3.0"),sQuery(id+"F0.wireOp",EDGE,"E4.2.4.0"),sQuery(id+"F0.wireOp",EDGE,"E4.3.4.0"),sQuery(id+"F0.wireOp",EDGE,"E4.2.5.0"),sQuery(id+"F0.wireOp",EDGE,"E4.3.5.0"),sQuery(id+"F0.wireOp",EDGE,"E5.2.6.0"),sQuery(id+"F0.wireOp",EDGE,"E5.3.6.0"),sQuery(id+"F0.wireOp",EDGE,"E5.2.7.0"),sQuery(id+"F0.wireOp",EDGE,"E5.3.7.0"),subQ1,subQ0,sQuery(id+"F0.wireOp",EDGE,"E6.2.9.0"),sQuery(id+"F0.wireOp",EDGE,"E6.3.9.0")])],"isStart":false})]});}
            var Q14;
            {var subQ0=sQuery(id+"F0.wireOp",EDGE,"E5.3.7.0");var subQ1=sQuery(id+"F0.wireOp",EDGE,"E5.2.7.0");Q14=makeQuery(id+"F2.opChamfer","BLEND_EDGE",EDGE,{"blendedFrom":[makeQuery(id+"F1.opExtrude","SWEPT_EDGE",EDGE,{"disambiguationData":[OSD([subQ1,subQ0])]}),makeQuery(id+"F1.opExtrude","CAP_FACE",FACE,{"disambiguationData":[OSD([sQuery(id+"F0.wireOp",EDGE,"E0"),sQuery(id+"F0.wireOp",EDGE,"E1"),sQuery(id+"F0.wireOp",EDGE,"E2.MirrorCS"),sQuery(id+"F0.wireOp",EDGE,"E3.1.0"),sQuery(id+"F0.wireOp",EDGE,"E3.1.1"),sQuery(id+"F0.wireOp",EDGE,"E3.2.0"),sQuery(id+"F0.wireOp",EDGE,"E3.2.1"),sQuery(id+"F0.wireOp",EDGE,"E4.2.3.0"),sQuery(id+"F0.wireOp",EDGE,"E4.3.3.0"),sQuery(id+"F0.wireOp",EDGE,"E4.2.4.0"),sQuery(id+"F0.wireOp",EDGE,"E4.3.4.0"),sQuery(id+"F0.wireOp",EDGE,"E4.2.5.0"),sQuery(id+"F0.wireOp",EDGE,"E4.3.5.0"),sQuery(id+"F0.wireOp",EDGE,"E5.2.6.0"),sQuery(id+"F0.wireOp",EDGE,"E5.3.6.0"),subQ1,subQ0,sQuery(id+"F0.wireOp",EDGE,"E6.2.8.0"),sQuery(id+"F0.wireOp",EDGE,"E6.3.8.0"),sQuery(id+"F0.wireOp",EDGE,"E6.2.9.0"),sQuery(id+"F0.wireOp",EDGE,"E6.3.9.0")])],"isStart":false})],"blendedInto":[makeQuery(id+"F1.opExtrude","CAP_FACE",FACE,{"disambiguationData":[OSD([sQuery(id+"F0.wireOp",EDGE,"E0"),sQuery(id+"F0.wireOp",EDGE,"E1"),sQuery(id+"F0.wireOp",EDGE,"E2.MirrorCS"),sQuery(id+"F0.wireOp",EDGE,"E3.1.0"),sQuery(id+"F0.wireOp",EDGE,"E3.1.1"),sQuery(id+"F0.wireOp",EDGE,"E3.2.0"),sQuery(id+"F0.wireOp",EDGE,"E3.2.1"),sQuery(id+"F0.wireOp",EDGE,"E4.2.3.0"),sQuery(id+"F0.wireOp",EDGE,"E4.3.3.0"),sQuery(id+"F0.wireOp",EDGE,"E4.2.4.0"),sQuery(id+"F0.wireOp",EDGE,"E4.3.4.0"),sQuery(id+"F0.wireOp",EDGE,"E4.2.5.0"),sQuery(id+"F0.wireOp",EDGE,"E4.3.5.0"),sQuery(id+"F0.wireOp",EDGE,"E5.2.6.0"),sQuery(id+"F0.wireOp",EDGE,"E5.3.6.0"),subQ1,subQ0,sQuery(id+"F0.wireOp",EDGE,"E6.2.8.0"),sQuery(id+"F0.wireOp",EDGE,"E6.3.8.0"),sQuery(id+"F0.wireOp",EDGE,"E6.2.9.0"),sQuery(id+"F0.wireOp",EDGE,"E6.3.9.0")])],"isStart":false})]});}
            var Q15;
            {var subQ0=sQuery(id+"F0.wireOp",EDGE,"E5.3.6.0");var subQ1=sQuery(id+"F0.wireOp",EDGE,"E5.2.6.0");Q15=makeQuery(id+"F2.opChamfer","BLEND_EDGE",EDGE,{"blendedFrom":[makeQuery(id+"F1.opExtrude","SWEPT_EDGE",EDGE,{"disambiguationData":[OSD([subQ1,subQ0])]}),makeQuery(id+"F1.opExtrude","CAP_FACE",FACE,{"disambiguationData":[OSD([sQuery(id+"F0.wireOp",EDGE,"E0"),sQuery(id+"F0.wireOp",EDGE,"E1"),sQuery(id+"F0.wireOp",EDGE,"E2.MirrorCS"),sQuery(id+"F0.wireOp",EDGE,"E3.1.0"),sQuery(id+"F0.wireOp",EDGE,"E3.1.1"),sQuery(id+"F0.wireOp",EDGE,"E3.2.0"),sQuery(id+"F0.wireOp",EDGE,"E3.2.1"),sQuery(id+"F0.wireOp",EDGE,"E4.2.3.0"),sQuery(id+"F0.wireOp",EDGE,"E4.3.3.0"),sQuery(id+"F0.wireOp",EDGE,"E4.2.4.0"),sQuery(id+"F0.wireOp",EDGE,"E4.3.4.0"),sQuery(id+"F0.wireOp",EDGE,"E4.2.5.0"),sQuery(id+"F0.wireOp",EDGE,"E4.3.5.0"),subQ1,subQ0,sQuery(id+"F0.wireOp",EDGE,"E5.2.7.0"),sQuery(id+"F0.wireOp",EDGE,"E5.3.7.0"),sQuery(id+"F0.wireOp",EDGE,"E6.2.8.0"),sQuery(id+"F0.wireOp",EDGE,"E6.3.8.0"),sQuery(id+"F0.wireOp",EDGE,"E6.2.9.0"),sQuery(id+"F0.wireOp",EDGE,"E6.3.9.0")])],"isStart":false})],"blendedInto":[makeQuery(id+"F1.opExtrude","CAP_FACE",FACE,{"disambiguationData":[OSD([sQuery(id+"F0.wireOp",EDGE,"E0"),sQuery(id+"F0.wireOp",EDGE,"E1"),sQuery(id+"F0.wireOp",EDGE,"E2.MirrorCS"),sQuery(id+"F0.wireOp",EDGE,"E3.1.0"),sQuery(id+"F0.wireOp",EDGE,"E3.1.1"),sQuery(id+"F0.wireOp",EDGE,"E3.2.0"),sQuery(id+"F0.wireOp",EDGE,"E3.2.1"),sQuery(id+"F0.wireOp",EDGE,"E4.2.3.0"),sQuery(id+"F0.wireOp",EDGE,"E4.3.3.0"),sQuery(id+"F0.wireOp",EDGE,"E4.2.4.0"),sQuery(id+"F0.wireOp",EDGE,"E4.3.4.0"),sQuery(id+"F0.wireOp",EDGE,"E4.2.5.0"),sQuery(id+"F0.wireOp",EDGE,"E4.3.5.0"),subQ1,subQ0,sQuery(id+"F0.wireOp",EDGE,"E5.2.7.0"),sQuery(id+"F0.wireOp",EDGE,"E5.3.7.0"),sQuery(id+"F0.wireOp",EDGE,"E6.2.8.0"),sQuery(id+"F0.wireOp",EDGE,"E6.3.8.0"),sQuery(id+"F0.wireOp",EDGE,"E6.2.9.0"),sQuery(id+"F0.wireOp",EDGE,"E6.3.9.0")])],"isStart":false})]});}
            var Q16;
            {var subQ0=sQuery(id+"F0.wireOp",EDGE,"E6.3.9.0");var subQ1=sQuery(id+"F0.wireOp",EDGE,"E6.2.9.0");Q16=makeQuery(id+"F2.opChamfer","BLEND_EDGE",EDGE,{"blendedFrom":[makeQuery(id+"F1.opExtrude","SWEPT_EDGE",EDGE,{"disambiguationData":[OSD([subQ1,subQ0])]}),makeQuery(id+"F1.opExtrude","CAP_FACE",FACE,{"disambiguationData":[OSD([sQuery(id+"F0.wireOp",EDGE,"E0"),sQuery(id+"F0.wireOp",EDGE,"E1"),sQuery(id+"F0.wireOp",EDGE,"E2.MirrorCS"),sQuery(id+"F0.wireOp",EDGE,"E3.1.0"),sQuery(id+"F0.wireOp",EDGE,"E3.1.1"),sQuery(id+"F0.wireOp",EDGE,"E3.2.0"),sQuery(id+"F0.wireOp",EDGE,"E3.2.1"),sQuery(id+"F0.wireOp",EDGE,"E4.2.3.0"),sQuery(id+"F0.wireOp",EDGE,"E4.3.3.0"),sQuery(id+"F0.wireOp",EDGE,"E4.2.4.0"),sQuery(id+"F0.wireOp",EDGE,"E4.3.4.0"),sQuery(id+"F0.wireOp",EDGE,"E4.2.5.0"),sQuery(id+"F0.wireOp",EDGE,"E4.3.5.0"),sQuery(id+"F0.wireOp",EDGE,"E5.2.6.0"),sQuery(id+"F0.wireOp",EDGE,"E5.3.6.0"),sQuery(id+"F0.wireOp",EDGE,"E5.2.7.0"),sQuery(id+"F0.wireOp",EDGE,"E5.3.7.0"),sQuery(id+"F0.wireOp",EDGE,"E6.2.8.0"),sQuery(id+"F0.wireOp",EDGE,"E6.3.8.0"),subQ1,subQ0])],"isStart":true})],"blendedInto":[makeQuery(id+"F1.opExtrude","CAP_FACE",FACE,{"disambiguationData":[OSD([sQuery(id+"F0.wireOp",EDGE,"E0"),sQuery(id+"F0.wireOp",EDGE,"E1"),sQuery(id+"F0.wireOp",EDGE,"E2.MirrorCS"),sQuery(id+"F0.wireOp",EDGE,"E3.1.0"),sQuery(id+"F0.wireOp",EDGE,"E3.1.1"),sQuery(id+"F0.wireOp",EDGE,"E3.2.0"),sQuery(id+"F0.wireOp",EDGE,"E3.2.1"),sQuery(id+"F0.wireOp",EDGE,"E4.2.3.0"),sQuery(id+"F0.wireOp",EDGE,"E4.3.3.0"),sQuery(id+"F0.wireOp",EDGE,"E4.2.4.0"),sQuery(id+"F0.wireOp",EDGE,"E4.3.4.0"),sQuery(id+"F0.wireOp",EDGE,"E4.2.5.0"),sQuery(id+"F0.wireOp",EDGE,"E4.3.5.0"),sQuery(id+"F0.wireOp",EDGE,"E5.2.6.0"),sQuery(id+"F0.wireOp",EDGE,"E5.3.6.0"),sQuery(id+"F0.wireOp",EDGE,"E5.2.7.0"),sQuery(id+"F0.wireOp",EDGE,"E5.3.7.0"),sQuery(id+"F0.wireOp",EDGE,"E6.2.8.0"),sQuery(id+"F0.wireOp",EDGE,"E6.3.8.0"),subQ1,subQ0])],"isStart":true})]});}
            var Q17;
            {var subQ0=sQuery(id+"F0.wireOp",EDGE,"E6.3.8.0");var subQ1=sQuery(id+"F0.wireOp",EDGE,"E6.2.8.0");Q17=makeQuery(id+"F2.opChamfer","BLEND_EDGE",EDGE,{"blendedFrom":[makeQuery(id+"F1.opExtrude","SWEPT_EDGE",EDGE,{"disambiguationData":[OSD([subQ1,subQ0])]}),makeQuery(id+"F1.opExtrude","CAP_FACE",FACE,{"disambiguationData":[OSD([sQuery(id+"F0.wireOp",EDGE,"E0"),sQuery(id+"F0.wireOp",EDGE,"E1"),sQuery(id+"F0.wireOp",EDGE,"E2.MirrorCS"),sQuery(id+"F0.wireOp",EDGE,"E3.1.0"),sQuery(id+"F0.wireOp",EDGE,"E3.1.1"),sQuery(id+"F0.wireOp",EDGE,"E3.2.0"),sQuery(id+"F0.wireOp",EDGE,"E3.2.1"),sQuery(id+"F0.wireOp",EDGE,"E4.2.3.0"),sQuery(id+"F0.wireOp",EDGE,"E4.3.3.0"),sQuery(id+"F0.wireOp",EDGE,"E4.2.4.0"),sQuery(id+"F0.wireOp",EDGE,"E4.3.4.0"),sQuery(id+"F0.wireOp",EDGE,"E4.2.5.0"),sQuery(id+"F0.wireOp",EDGE,"E4.3.5.0"),sQuery(id+"F0.wireOp",EDGE,"E5.2.6.0"),sQuery(id+"F0.wireOp",EDGE,"E5.3.6.0"),sQuery(id+"F0.wireOp",EDGE,"E5.2.7.0"),sQuery(id+"F0.wireOp",EDGE,"E5.3.7.0"),subQ1,subQ0,sQuery(id+"F0.wireOp",EDGE,"E6.2.9.0"),sQuery(id+"F0.wireOp",EDGE,"E6.3.9.0")])],"isStart":true})],"blendedInto":[makeQuery(id+"F1.opExtrude","CAP_FACE",FACE,{"disambiguationData":[OSD([sQuery(id+"F0.wireOp",EDGE,"E0"),sQuery(id+"F0.wireOp",EDGE,"E1"),sQuery(id+"F0.wireOp",EDGE,"E2.MirrorCS"),sQuery(id+"F0.wireOp",EDGE,"E3.1.0"),sQuery(id+"F0.wireOp",EDGE,"E3.1.1"),sQuery(id+"F0.wireOp",EDGE,"E3.2.0"),sQuery(id+"F0.wireOp",EDGE,"E3.2.1"),sQuery(id+"F0.wireOp",EDGE,"E4.2.3.0"),sQuery(id+"F0.wireOp",EDGE,"E4.3.3.0"),sQuery(id+"F0.wireOp",EDGE,"E4.2.4.0"),sQuery(id+"F0.wireOp",EDGE,"E4.3.4.0"),sQuery(id+"F0.wireOp",EDGE,"E4.2.5.0"),sQuery(id+"F0.wireOp",EDGE,"E4.3.5.0"),sQuery(id+"F0.wireOp",EDGE,"E5.2.6.0"),sQuery(id+"F0.wireOp",EDGE,"E5.3.6.0"),sQuery(id+"F0.wireOp",EDGE,"E5.2.7.0"),sQuery(id+"F0.wireOp",EDGE,"E5.3.7.0"),subQ1,subQ0,sQuery(id+"F0.wireOp",EDGE,"E6.2.9.0"),sQuery(id+"F0.wireOp",EDGE,"E6.3.9.0")])],"isStart":true})]});}
            var Q18;
            {var subQ0=sQuery(id+"F0.wireOp",EDGE,"E5.3.7.0");var subQ1=sQuery(id+"F0.wireOp",EDGE,"E5.2.7.0");Q18=makeQuery(id+"F2.opChamfer","BLEND_EDGE",EDGE,{"blendedFrom":[makeQuery(id+"F1.opExtrude","SWEPT_EDGE",EDGE,{"disambiguationData":[OSD([subQ1,subQ0])]}),makeQuery(id+"F1.opExtrude","CAP_FACE",FACE,{"disambiguationData":[OSD([sQuery(id+"F0.wireOp",EDGE,"E0"),sQuery(id+"F0.wireOp",EDGE,"E1"),sQuery(id+"F0.wireOp",EDGE,"E2.MirrorCS"),sQuery(id+"F0.wireOp",EDGE,"E3.1.0"),sQuery(id+"F0.wireOp",EDGE,"E3.1.1"),sQuery(id+"F0.wireOp",EDGE,"E3.2.0"),sQuery(id+"F0.wireOp",EDGE,"E3.2.1"),sQuery(id+"F0.wireOp",EDGE,"E4.2.3.0"),sQuery(id+"F0.wireOp",EDGE,"E4.3.3.0"),sQuery(id+"F0.wireOp",EDGE,"E4.2.4.0"),sQuery(id+"F0.wireOp",EDGE,"E4.3.4.0"),sQuery(id+"F0.wireOp",EDGE,"E4.2.5.0"),sQuery(id+"F0.wireOp",EDGE,"E4.3.5.0"),sQuery(id+"F0.wireOp",EDGE,"E5.2.6.0"),sQuery(id+"F0.wireOp",EDGE,"E5.3.6.0"),subQ1,subQ0,sQuery(id+"F0.wireOp",EDGE,"E6.2.8.0"),sQuery(id+"F0.wireOp",EDGE,"E6.3.8.0"),sQuery(id+"F0.wireOp",EDGE,"E6.2.9.0"),sQuery(id+"F0.wireOp",EDGE,"E6.3.9.0")])],"isStart":true})],"blendedInto":[makeQuery(id+"F1.opExtrude","CAP_FACE",FACE,{"disambiguationData":[OSD([sQuery(id+"F0.wireOp",EDGE,"E0"),sQuery(id+"F0.wireOp",EDGE,"E1"),sQuery(id+"F0.wireOp",EDGE,"E2.MirrorCS"),sQuery(id+"F0.wireOp",EDGE,"E3.1.0"),sQuery(id+"F0.wireOp",EDGE,"E3.1.1"),sQuery(id+"F0.wireOp",EDGE,"E3.2.0"),sQuery(id+"F0.wireOp",EDGE,"E3.2.1"),sQuery(id+"F0.wireOp",EDGE,"E4.2.3.0"),sQuery(id+"F0.wireOp",EDGE,"E4.3.3.0"),sQuery(id+"F0.wireOp",EDGE,"E4.2.4.0"),sQuery(id+"F0.wireOp",EDGE,"E4.3.4.0"),sQuery(id+"F0.wireOp",EDGE,"E4.2.5.0"),sQuery(id+"F0.wireOp",EDGE,"E4.3.5.0"),sQuery(id+"F0.wireOp",EDGE,"E5.2.6.0"),sQuery(id+"F0.wireOp",EDGE,"E5.3.6.0"),subQ1,subQ0,sQuery(id+"F0.wireOp",EDGE,"E6.2.8.0"),sQuery(id+"F0.wireOp",EDGE,"E6.3.8.0"),sQuery(id+"F0.wireOp",EDGE,"E6.2.9.0"),sQuery(id+"F0.wireOp",EDGE,"E6.3.9.0")])],"isStart":true})]});}
            var Q19;
            {var subQ0=sQuery(id+"F0.wireOp",EDGE,"E5.3.6.0");var subQ1=sQuery(id+"F0.wireOp",EDGE,"E5.2.6.0");Q19=makeQuery(id+"F2.opChamfer","BLEND_EDGE",EDGE,{"blendedFrom":[makeQuery(id+"F1.opExtrude","SWEPT_EDGE",EDGE,{"disambiguationData":[OSD([subQ1,subQ0])]}),makeQuery(id+"F1.opExtrude","CAP_FACE",FACE,{"disambiguationData":[OSD([sQuery(id+"F0.wireOp",EDGE,"E0"),sQuery(id+"F0.wireOp",EDGE,"E1"),sQuery(id+"F0.wireOp",EDGE,"E2.MirrorCS"),sQuery(id+"F0.wireOp",EDGE,"E3.1.0"),sQuery(id+"F0.wireOp",EDGE,"E3.1.1"),sQuery(id+"F0.wireOp",EDGE,"E3.2.0"),sQuery(id+"F0.wireOp",EDGE,"E3.2.1"),sQuery(id+"F0.wireOp",EDGE,"E4.2.3.0"),sQuery(id+"F0.wireOp",EDGE,"E4.3.3.0"),sQuery(id+"F0.wireOp",EDGE,"E4.2.4.0"),sQuery(id+"F0.wireOp",EDGE,"E4.3.4.0"),sQuery(id+"F0.wireOp",EDGE,"E4.2.5.0"),sQuery(id+"F0.wireOp",EDGE,"E4.3.5.0"),subQ1,subQ0,sQuery(id+"F0.wireOp",EDGE,"E5.2.7.0"),sQuery(id+"F0.wireOp",EDGE,"E5.3.7.0"),sQuery(id+"F0.wireOp",EDGE,"E6.2.8.0"),sQuery(id+"F0.wireOp",EDGE,"E6.3.8.0"),sQuery(id+"F0.wireOp",EDGE,"E6.2.9.0"),sQuery(id+"F0.wireOp",EDGE,"E6.3.9.0")])],"isStart":true})],"blendedInto":[makeQuery(id+"F1.opExtrude","CAP_FACE",FACE,{"disambiguationData":[OSD([sQuery(id+"F0.wireOp",EDGE,"E0"),sQuery(id+"F0.wireOp",EDGE,"E1"),sQuery(id+"F0.wireOp",EDGE,"E2.MirrorCS"),sQuery(id+"F0.wireOp",EDGE,"E3.1.0"),sQuery(id+"F0.wireOp",EDGE,"E3.1.1"),sQuery(id+"F0.wireOp",EDGE,"E3.2.0"),sQuery(id+"F0.wireOp",EDGE,"E3.2.1"),sQuery(id+"F0.wireOp",EDGE,"E4.2.3.0"),sQuery(id+"F0.wireOp",EDGE,"E4.3.3.0"),sQuery(id+"F0.wireOp",EDGE,"E4.2.4.0"),sQuery(id+"F0.wireOp",EDGE,"E4.3.4.0"),sQuery(id+"F0.wireOp",EDGE,"E4.2.5.0"),sQuery(id+"F0.wireOp",EDGE,"E4.3.5.0"),subQ1,subQ0,sQuery(id+"F0.wireOp",EDGE,"E5.2.7.0"),sQuery(id+"F0.wireOp",EDGE,"E5.3.7.0"),sQuery(id+"F0.wireOp",EDGE,"E6.2.8.0"),sQuery(id+"F0.wireOp",EDGE,"E6.3.8.0"),sQuery(id+"F0.wireOp",EDGE,"E6.2.9.0"),sQuery(id+"F0.wireOp",EDGE,"E6.3.9.0")])],"isStart":true})]});}
            chamfer(context, id + "F3", {"entities" : qUnion([Q0, Q1, Q2, Q3, Q4, Q5, Q6, Q7, Q8, Q9, Q10, Q11, Q12, Q13, Q14, Q15, Q16, Q17, Q18, Q19]), "width" : 4 * mm, "tangentPropagation" : true});
        }
        {
            var Q0;
            Q0=makeQuery(id+"F1.opExtrude","CAP_FACE",FACE,{"disambiguationData":[OSD([sQuery(id+"F0.wireOp",EDGE,"E0"),sQuery(id+"F0.wireOp",EDGE,"E1"),sQuery(id+"F0.wireOp",EDGE,"E2.MirrorCS"),sQuery(id+"F0.wireOp",EDGE,"E3.1.0"),sQuery(id+"F0.wireOp",EDGE,"E3.1.1"),sQuery(id+"F0.wireOp",EDGE,"E3.2.0"),sQuery(id+"F0.wireOp",EDGE,"E3.2.1"),sQuery(id+"F0.wireOp",EDGE,"E4.2.3.0"),sQuery(id+"F0.wireOp",EDGE,"E4.3.3.0"),sQuery(id+"F0.wireOp",EDGE,"E4.2.4.0"),sQuery(id+"F0.wireOp",EDGE,"E4.3.4.0"),sQuery(id+"F0.wireOp",EDGE,"E4.2.5.0"),sQuery(id+"F0.wireOp",EDGE,"E4.3.5.0")])],"isStart":false});
            var sketch = newSketch(context, id + "F4", { "sketchPlane" : qUnion([Q0])});
            skArc(sketch, "E7.0", {"start": v(1.19, -1.05) * mm, "mid": v(0, 1.62) * mm, "end": v(-1.2, -1.04) * mm});
            skLineSegment(sketch, "E8", {"start": v(-1.2, -1.04) * mm, "end": v(1.19, -1.05) * mm});
            skSolve(sketch);
        }
        {
            var Q0;
            Q0=qSketchRegion(id+"F4",true);
            extrude(context, id + "F5", {"entities" : qUnion([Q0]), "operationType" : NewBodyOperationType.REMOVE, "oppositeDirection" : true, "depth" : 25.4 * mm});
        }
        {
            var Q0;
            Q0=makeQuery(id+"F1.opExtrude","CAP_FACE",FACE,{"disambiguationData":[OSD([sQuery(id+"F0.wireOp",EDGE,"E0"),sQuery(id+"F0.wireOp",EDGE,"E1"),sQuery(id+"F0.wireOp",EDGE,"E2.MirrorCS"),sQuery(id+"F0.wireOp",EDGE,"E3.1.0"),sQuery(id+"F0.wireOp",EDGE,"E3.1.1"),sQuery(id+"F0.wireOp",EDGE,"E3.2.0"),sQuery(id+"F0.wireOp",EDGE,"E3.2.1"),sQuery(id+"F0.wireOp",EDGE,"E4.2.3.0"),sQuery(id+"F0.wireOp",EDGE,"E4.3.3.0"),sQuery(id+"F0.wireOp",EDGE,"E4.2.4.0"),sQuery(id+"F0.wireOp",EDGE,"E4.3.4.0"),sQuery(id+"F0.wireOp",EDGE,"E4.2.5.0"),sQuery(id+"F0.wireOp",EDGE,"E4.3.5.0"),sQuery(id+"F0.wireOp",EDGE,"E5.2.6.0"),sQuery(id+"F0.wireOp",EDGE,"E5.3.6.0"),sQuery(id+"F0.wireOp",EDGE,"E5.2.7.0"),sQuery(id+"F0.wireOp",EDGE,"E5.3.7.0"),sQuery(id+"F0.wireOp",EDGE,"E6.2.8.0"),sQuery(id+"F0.wireOp",EDGE,"E6.3.8.0"),sQuery(id+"F0.wireOp",EDGE,"E6.2.9.0"),sQuery(id+"F0.wireOp",EDGE,"E6.3.9.0")])],"isStart":false});
            var sketch = newSketch(context, id + "F6", { "sketchPlane" : qUnion([Q0])});
            skLineSegment(sketch, "E9", {"start": v(0, 1.62) * mm, "end": v(0, 4.16) * mm});
            skLineSegment(sketch, "E10.0", {"start": v(0.32, 1.56) * mm, "end": v(0.32, 5.91) * mm});
            skLineSegment(sketch, "E11.0", {"start": v(-0.32, 1.6) * mm, "end": v(-0.32, 5.91) * mm});
            skLineSegment(sketch, "E12", {"start": v(-0.32, 5.91) * mm, "end": v(0.32, 5.91) * mm});
            skSolve(sketch);
        }
        {
            var Q0;
            {var subQ4=sQuery(id+"F6.wireOp",EDGE,"ygnr69zs-SGs4-EEnQ-L1pw-wUKNl8bqFLjY");Q0=makeQuery(id+"F6.imprint","IMPRINT",FACE,{"disambiguationData":[TD([[makeQuery(id+"F6.imprint","IMPRINT",EDGE,{"derivedFrom":subQ4}),-1.0]])]});}
            var Q1;
            {var subQ2=sQuery(id+"F6.wireOp",EDGE,"E11.0");Q1=makeQuery(id+"F6.imprint","IMPRINT",FACE,{"disambiguationData":[TD([[makeQuery(id+"F6.imprint","IMPRINT",EDGE,{"derivedFrom":subQ2}),-1.0]])]});}
            extrude(context, id + "F7", {"entities" : qUnion([Q0, Q1]), "operationType" : NewBodyOperationType.REMOVE, "oppositeDirection" : true, "depth" : 25.4 * mm});
        }
        {
            var Q0;
            Q0=makeQuery(id+"F1.opExtrude","CAP_FACE",FACE,{"disambiguationData":[OSD([sQuery(id+"F0.wireOp",EDGE,"E0"),sQuery(id+"F0.wireOp",EDGE,"E1"),sQuery(id+"F0.wireOp",EDGE,"E2.MirrorCS"),sQuery(id+"F0.wireOp",EDGE,"E3.1.0"),sQuery(id+"F0.wireOp",EDGE,"E3.1.1"),sQuery(id+"F0.wireOp",EDGE,"E3.2.0"),sQuery(id+"F0.wireOp",EDGE,"E3.2.1"),sQuery(id+"F0.wireOp",EDGE,"E4.2.3.0"),sQuery(id+"F0.wireOp",EDGE,"E4.3.3.0"),sQuery(id+"F0.wireOp",EDGE,"E4.2.4.0"),sQuery(id+"F0.wireOp",EDGE,"E4.3.4.0"),sQuery(id+"F0.wireOp",EDGE,"E4.2.5.0"),sQuery(id+"F0.wireOp",EDGE,"E4.3.5.0"),sQuery(id+"F0.wireOp",EDGE,"E5.2.6.0"),sQuery(id+"F0.wireOp",EDGE,"E5.3.6.0"),sQuery(id+"F0.wireOp",EDGE,"E5.2.7.0"),sQuery(id+"F0.wireOp",EDGE,"E5.3.7.0"),sQuery(id+"F0.wireOp",EDGE,"E6.2.8.0"),sQuery(id+"F0.wireOp",EDGE,"E6.3.8.0"),sQuery(id+"F0.wireOp",EDGE,"E6.2.9.0"),sQuery(id+"F0.wireOp",EDGE,"E6.3.9.0")])],"isStart":false});
            var sketch = newSketch(context, id + "F8", { "sketchPlane" : qUnion([Q0])});
            skCircle(sketch, "E13", {"center": v(0, 0) * mm, "radius": 3.18 * mm});
            skCircle(sketch, "E14", {"center": v(0, 0) * mm, "radius": 14.6 * mm});
            skSolve(sketch);
        }
        {
            var Q0;
            {var subQ5=makeQuery(id+"F7.boolean.opBoolean","COPY",EDGE,{"derivedFrom":makeQuery(id+"F7.opExtrude","CAP_EDGE",EDGE,{"disambiguationData":[OSD([sQuery(id+"F6.wireOp",EDGE,"E12")])],"isStart":true})});Q0=makeQuery(id+"F8.imprint","IMPRINT",FACE,{"disambiguationData":[TD([[makeQuery(id+"F8.imprint","IMPRINT",EDGE,{"derivedFrom":subQ5}),-1.0]])]});}
            var Q1;
            Q1=makeQuery(id+"F8.imprint","IMPRINT",FACE,{"disambiguationData":[TD([[makeQuery(id+"F8.imprint","IMPRINT",EDGE,{"derivedFrom":sQuery(id+"F8.wireOp",EDGE,"E14")}),1.0]])]});
            extrude(context, id + "F9", {"entities" : qUnion([Q0, Q1]), "operationType" : NewBodyOperationType.REMOVE, "oppositeDirection" : true, "depth" : 3.17 * mm});
        }
        {
            var Q0;
            Q0=makeQuery(id+"F9.boolean.opBoolean","COPY",EDGE,{"derivedFrom":makeQuery(id+"F9.opExtrude","CAP_EDGE",EDGE,{"disambiguationData":[OSD([sQuery(id+"F8.wireOp",EDGE,"E13")])],"isStart":false})});
            chamfer(context, id + "F10", {"entities" : qUnion([Q0]), "width" : 3.17 * mm, "tangentPropagation" : true});
        }
    });
